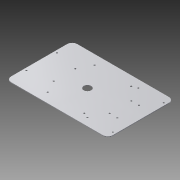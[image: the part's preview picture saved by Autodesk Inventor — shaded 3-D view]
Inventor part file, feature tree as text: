
AUTODESK INVENTOR PART (.ipt)
format: ipt  version: 2015 (Build 190159000, 159)  size: 175,616 bytes
history: native  units: mm
features: sketch x7, extrude x4, hole x3, other x1, fillet x1
ambient origin geometry x8: Origin, YZ Plane, XZ Plane, XY Plane, X Axis, Y Axis, Z Axis, Center Point
bodies: Body1 (feature_tree)
feature tree (16):
  other  "ソリッド1"
  extrude  "押し出し1"  Depth=240.0mm
  hole  "穴1"  [1 undecoded]
  hole  "穴2"  [1 undecoded]
  extrude  "押し出し2"  Depth=50.0mm
  extrude  "押し出し3"  Depth=53.75mm
  extrude  "押し出し4"  Depth=50.0mm
  fillet  "フィレット1"  Radius=53.75mm
  hole  "穴3"  [1 undecoded]
  sketch  "スケッチ1"
  sketch  "スケッチ2"
  sketch  "スケッチ4"
  sketch  "スケッチ5"
  sketch  "スケッチ6"
  sketch  "スケッチ7"
  sketch  "スケッチ8"
note: 3 required parameter values undecoded (feature->parameter linkage not recoverable at this tier; creation-order binding heuristic only, values carry confidence <= 0.55)
